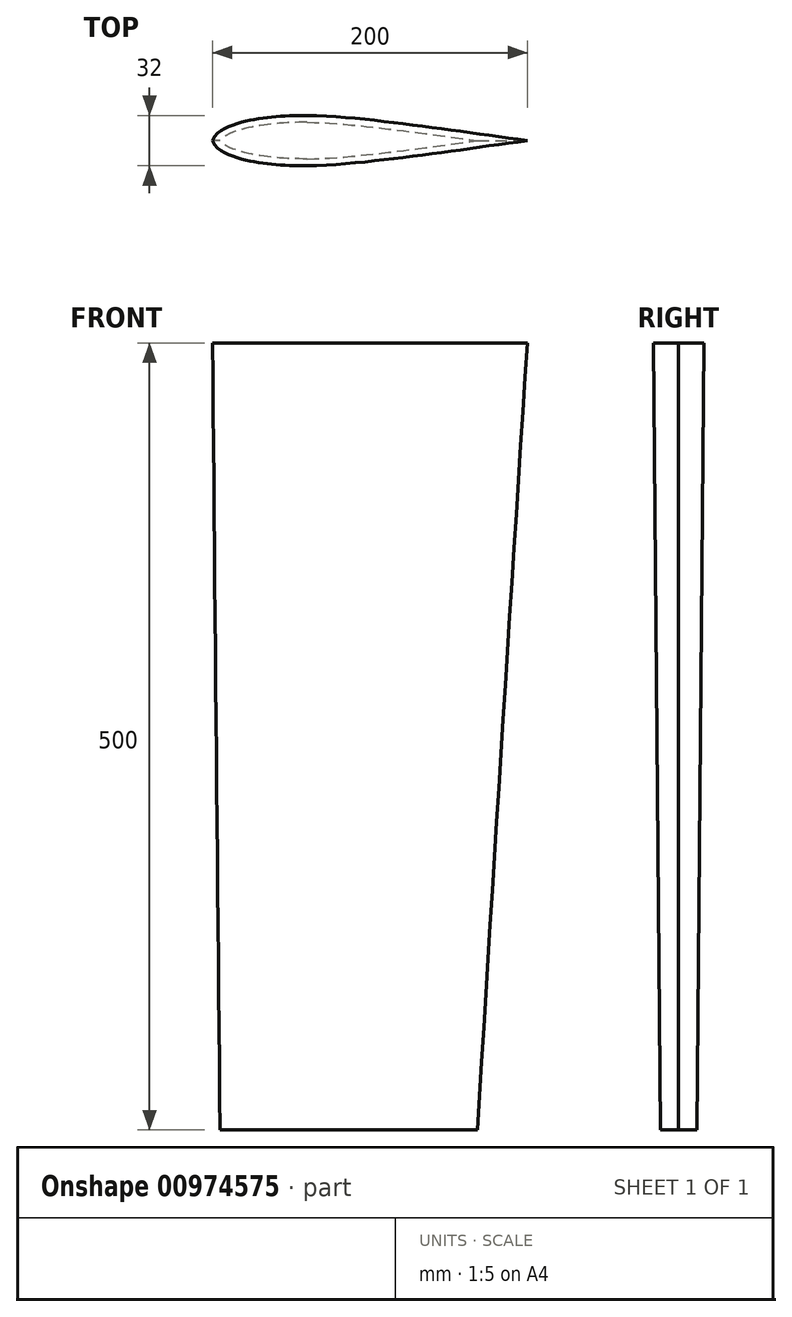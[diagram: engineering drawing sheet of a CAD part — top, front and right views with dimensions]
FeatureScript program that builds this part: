
annotation { "Feature Type Name" : "Feature", "Feature Type Description" : "" }
export const myFeature = defineFeature(function(context is Context, id is Id, definition is map)
    precondition{}
    {
        {
            var Q0;
            Q0=qCreatedBy(makeId("Top.planeOp"),FACE);
            cPlane(context, id + "F0", {"entities" : qUnion([Q0]), "cplaneType" : CPlaneType.OFFSET, "offset" : 100 * mm, "width" : 150 * mm, "height" : 150 * mm});
        }
        {
            var Q0;
            Q0=qCreatedBy(id+"F0.planeOp",FACE);
            var sketch = newSketch(context, id + "F1", { "sketchPlane" : qUnion([Q0])});
            skLineSegment(sketch, "E0", {"start": v(-60, 0) * mm, "end": v(0, 0) * mm, "construction": true});
            skLineSegment(sketch, "E1", {"start": v(0, 0) * mm, "end": v(140, 0) * mm, "construction": true});
            skLineSegment(sketch, "E2", {"start": v(0, -16) * mm, "end": v(0, 16) * mm, "construction": true});
            skLineSegment(sketch, "E3", {"start": v(0, 16) * mm, "end": v(30.56, 16) * mm, "construction": true});
            skFitSpline(sketch, "E4", {"points": [v(0, 16) * mm, v(140, 0) * mm], "startDerivative": vector(95.58, 0) * mm, "endDerivative": vector(104.63, -13.8) * mm});
            skFitSpline(sketch, "E5", {"points": [v(0, 16) * mm, v(-60, 0) * mm], "startDerivative": vector(-94.18, 0) * mm, "endDerivative": vector(-8.31, -30.97) * mm});
            skLineSegment(sketch, "E6", {"start": v(0, 16) * mm, "end": v(-18.53, 16) * mm, "construction": true});
            skPoint(sketch, "E7", {"position": v(15.28, 16) * mm});
            skFitSpline(sketch, "E8.MirrorCS", {"points": [v(0, -16) * mm, v(140, 0) * mm], "startDerivative": vector(95.58, 0) * mm, "endDerivative": vector(104.63, 13.8) * mm});
            skFitSpline(sketch, "E9.MirrorCS", {"points": [v(0, -16) * mm, v(-60, 0) * mm], "startDerivative": vector(-94.18, 0) * mm, "endDerivative": vector(-8.31, 30.97) * mm});
            skSolve(sketch);
        }
        {
            var Q0;
            Q0=makeQuery(id+"F1.imprint","IMPRINT",FACE,{"disambiguationData":[TD([[makeQuery(id+"F1.imprint","IMPRINT",EDGE,{"derivedFrom":sQuery(id+"F1.wireOp",EDGE,"E4")}),-1.0]])]});
            extrude(context, id + "F2", {"entities" : qUnion([Q0]), "depth" : -500 * mm, "offsetDistance" : 25 * mm, "hasDraft" : true, "draftAngle" : .5 * degree, "draftPullDirection" : true});
        }
    });
